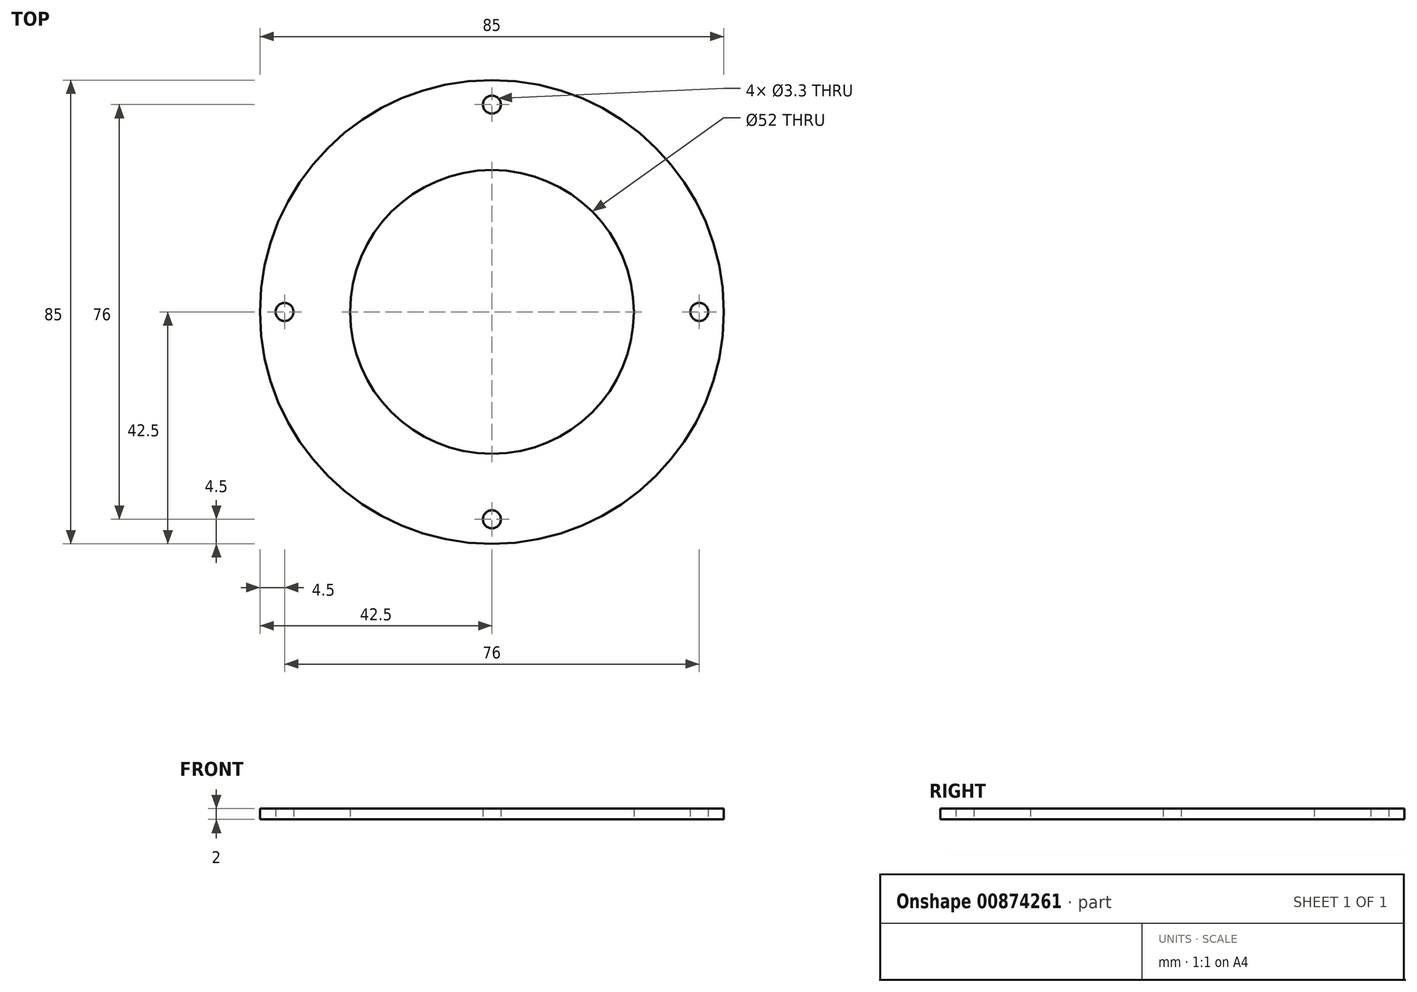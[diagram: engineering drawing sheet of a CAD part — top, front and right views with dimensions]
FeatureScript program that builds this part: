
annotation { "Feature Type Name" : "Feature", "Feature Type Description" : "" }
export const myFeature = defineFeature(function(context is Context, id is Id, definition is map)
    precondition{}
    {
        {
            var Q0;
            Q0=qCreatedBy(makeId("Top.planeOp"),FACE);
            var sketch = newSketch(context, id + "F0", { "sketchPlane" : qUnion([Q0])});
            skCircle(sketch, "E0", {"center": v(0, 0) * mm, "radius": 42.5 * mm});
            skCircle(sketch, "E1", {"center": v(0, 0) * mm, "radius": 26 * mm});
            skCircle(sketch, "E2", {"center": v(0, 38) * mm, "radius": 1.65 * mm});
            skLineSegment(sketch, "E3", {"start": v(0, 38) * mm, "end": v(0, 0) * mm, "construction": true});
            skLineSegment(sketch, "E4", {"start": v(0, 0) * mm, "end": v(0, -38) * mm, "construction": true});
            skCircle(sketch, "E5", {"center": v(0, -38) * mm, "radius": 1.65 * mm});
            skLineSegment(sketch, "E6", {"start": v(0, 0) * mm, "end": v(-38, 0) * mm, "construction": true});
            skLineSegment(sketch, "E7", {"start": v(0, 0) * mm, "end": v(38, 0) * mm, "construction": true});
            skCircle(sketch, "E8", {"center": v(38, 0) * mm, "radius": 1.65 * mm});
            skCircle(sketch, "E9", {"center": v(-38, 0) * mm, "radius": 1.65 * mm});
            skSolve(sketch);
        }
        {
            var Q0;
            Q0=makeQuery(id+"F0.imprint","IMPRINT",FACE,{"disambiguationData":[TD([[makeQuery(id+"F0.imprint","IMPRINT",EDGE,{"derivedFrom":sQuery(id+"F0.wireOp",EDGE,"E0")}),1.0]])]});
            extrude(context, id + "F1", {"entities" : qUnion([Q0]), "depth" : 2 * mm, "offsetDistance" : 25 * mm});
        }
    });
